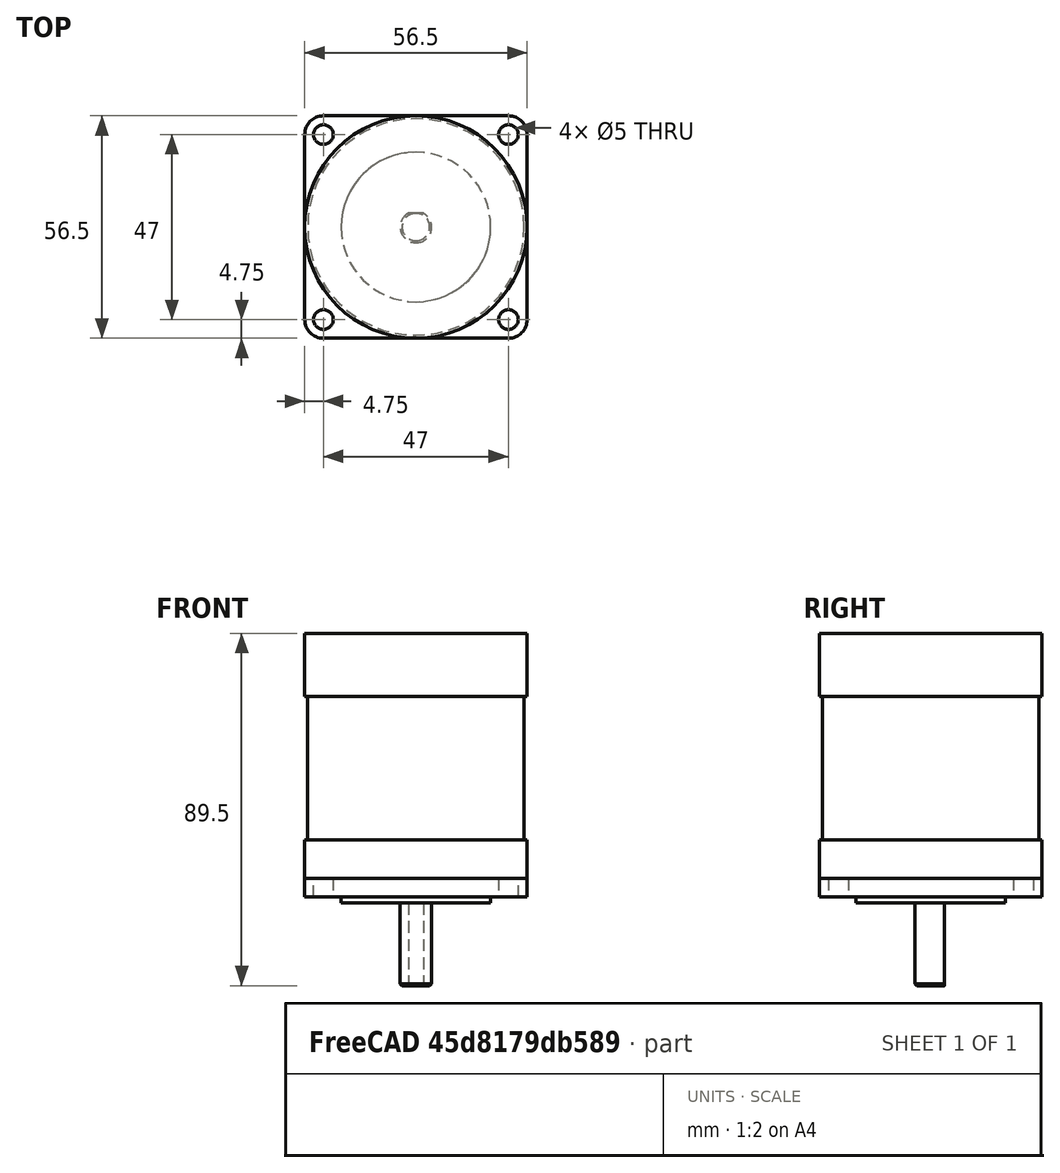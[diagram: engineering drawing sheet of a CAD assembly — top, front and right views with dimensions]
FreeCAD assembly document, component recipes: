
FREECAD ASSEMBLY — COMPONENT RECIPES ("57BLY-0730NBB")

This assembly document has 2 components, labeled P0..P1 below (a component is one placed body or linked part). 2 of them carry a construction recipe — the FreeCAD feature program that regenerates the part from scratch, quoted from this document or its linked companion documents; the rest are supplied as boundary geometry only. No exploded tour is included for this assembly.
COMPONENT P0 — recipe-attached ("57BLY-0730NBB", modeled in this document).
Construction recipe (the document's own serialized feature program — sketch geometry with constraints, then the solid features built on it; lengths are millimeters unless a unit is written):

FEATURE [Sketcher::SketchObject] Sketch
  FullyConstrained = true
  MapMode = 5
  Support = -> [XY_Plane]
  sketch-geometry (9):
    g0: LineSegment StartX=0 StartY=0 StartZ=0 EndX=28.25 EndY=0 EndZ=0
    g1: LineSegment StartX=28.25 StartY=0 StartZ=0 EndX=28.25 EndY=23.5386 EndZ=0
    g2: LineSegment StartX=23.5386 StartY=28.25 StartZ=0 EndX=0 EndY=28.25 EndZ=0
    g3: LineSegment StartX=0 StartY=28.25 StartZ=0 EndX=0 EndY=0 EndZ=0
    g4: ArcOfCircle CenterX=23.5386 CenterY=23.5386 CenterZ=0 NormalX=0 NormalY=0 NormalZ=1 AngleXU=0 Radius=4.71142 StartAngle=0 EndAngle=1.5708
    g5: GeomPoint X=28.25 Y=28.25 Z=0
    g6: Circle CenterX=23.5 CenterY=23.5 CenterZ=0 NormalX=0 NormalY=0 NormalZ=1 AngleXU=0 Radius=2.5
    g7: LineSegment StartX=0 StartY=0 StartZ=0 EndX=28.25 EndY=28.25 EndZ=0
    g8: GeomPoint X=26.8701 Y=26.8701 Z=0
  constraints (22):
    c: Coincident(g0,g1)
    c: Coincident(g2,g3)
    c: Coincident(g3,g0)
    c: Horizontal(g0)
    c: Horizontal(g2)
    c: Vertical(g1)
    c: Vertical(g3)
    c: Coincident(g0,g-1)
    c: Equal(g0,g3)
    c: PointOnObject(g5,g2)
    c: PointOnObject(g5,g1)
    c: Tangent(g2,g4) = -1.5708
    c: Tangent(g1,g4) = -1.5708
    c: Coincident(g7,g0)
    c: Coincident(g7,g5)
    c: PointOnObject(g6,g7)
    c: DistanceX(g6) = 23.5
    c: PointOnObject(g8,g4)
    c: PointOnObject(g8,g7)
    c: Distance(g0,g8) = 38
    c: DistanceX(g0) = 28.25  'width'
    c: Diameter(g6) = 5
FEATURE [PartDesign::Pad] Pad
  Direction = (0,0,1)
  Length = 4.7
  Length2 = 10
  Profile = -> Sketch
  ReferenceAxis = -> Sketch [N_Axis]
  Type = 0
FEATURE [PartDesign::Mirrored] Mirrored
  MirrorPlane = -> Sketch [V_Axis]
FEATURE [PartDesign::Mirrored] Mirrored001
  MirrorPlane = -> Sketch [H_Axis]
FEATURE [PartDesign::MultiTransform] MultiTransform
  BaseFeature = -> Pad
  Originals = -> [Pad]
  Transformations = -> [Mirrored,Mirrored001]
FEATURE [Sketcher::SketchObject] Sketch001
  FullyConstrained = true
  MapMode = 5
  Placement = pos=(0,0,0) rot=(1,0,0;1.5708rad)
  Support = -> [XZ_Plane]
  sketch-geometry (10):
    g0: LineSegment StartX=19 StartY=0 StartZ=0 EndX=28.25 EndY=0 EndZ=0
    g1: LineSegment StartX=28.25 StartY=0 StartZ=0 EndX=28.25 EndY=14.5 EndZ=0
    g2: LineSegment StartX=28.25 StartY=14.5 StartZ=0 EndX=27.5 EndY=14.5 EndZ=0
    g3: LineSegment StartX=27.5 StartY=14.5 StartZ=0 EndX=27.5 EndY=51 EndZ=0
    g4: LineSegment StartX=27.5 StartY=51 StartZ=0 EndX=28.25 EndY=51 EndZ=0
    g5: LineSegment StartX=28.25 StartY=51 StartZ=0 EndX=28.25 EndY=67 EndZ=0
    g6: LineSegment StartX=28.25 StartY=67 StartZ=0 EndX=0 EndY=67 EndZ=0
    g7: LineSegment StartX=0 StartY=67 StartZ=0 EndX=0 EndY=-1.5 EndZ=0
    g8: LineSegment StartX=19 StartY=0 StartZ=0 EndX=19 EndY=-1.5 EndZ=0
    g9: LineSegment StartX=19 StartY=-1.5 StartZ=0 EndX=0 EndY=-1.5 EndZ=0
  constraints (31):
    c: PointOnObject(g0,g-1)
    c: Coincident(g0,g1)
    c: Vertical(g1)
    c: Coincident(g1,g2)
    c: Horizontal(g2)
    c: Coincident(g2,g3)
    c: Vertical(g3)
    c: Coincident(g3,g4)
    c: Horizontal(g4)
    c: Coincident(g4,g5)
    c: Vertical(g5)
    c: Coincident(g5,g6)
    c: PointOnObject(g6,g-2)
    c: Horizontal(g6)
    c: Coincident(g6,g7)
    c: Distance(g1) = 14.5
    c: DistanceX(g2) = 27.5
    c: Distance(g3) = 36.5
    c: Vertical(g4,g1)
    c: Distance(g5) = 16
    c: Distance(g7) = 68.5  'total_height'
    c: Vertical(g8)
    c: Coincident(g9,g8)
    c: Horizontal(g9)
    c: DistanceX(g0) = 28.25
    c: Coincident(g0,g8)
    c: Distance(g9) = 19
    c: PointOnObject(g9,g-2)
    c: Coincident(g7,g9)
    c: DistanceY(g7,g-1) = 1.5  'bearing_height'
    c: Horizontal(g0)
FEATURE [PartDesign::Revolution] Revolution
  Angle = 360
  Axis = (0,-2e-16,1)
  Base = (0,0,0)
  BaseFeature = -> MultiTransform
  Profile = -> Sketch001
  ReferenceAxis = -> Sketch001 [V_Axis]
  Reversed = true
FEATURE [PartDesign::Body] Body
  Group = -> [Sketch,Pad,MultiTransform,Mirrored,Mirrored001,Sketch001,Revolution]
  Origin = -> Origin
  Tip = -> Revolution
FEATURE [Sketcher::SketchObject] Sketch002
  FullyConstrained = true
  MapMode = 5
  Support = -> [XY_Plane002]
  expr: .AttachmentOffset.Base.z = 0
  sketch-geometry (3):
    g0: LineSegment StartX=0 StartY=3.5 StartZ=0 EndX=1.93649 EndY=3.5 EndZ=0
    g1: ArcOfCircle CenterX=0 CenterY=0 CenterZ=0 NormalX=0 NormalY=0 NormalZ=1 AngleXU=0 Radius=4 StartAngle=4.71239 EndAngle=7.34862
    g2: LineSegment StartX=-7e-16 StartY=-4 StartZ=0 EndX=0 EndY=3.5 EndZ=0
  constraints (9):
    c: PointOnObject(g0,g-2)
    c: Horizontal(g0)
    c: Coincident(g1,g-1)
    c: PointOnObject(g1,g-2)
    c: Coincident(g1,g0)
    c: Coincident(g2,g1)
    c: Coincident(g2,g0)
    c: Distance(g2) = 7.5
    c: Diameter(g1) = 8
FEATURE [PartDesign::Pad] Pad001
  Direction = (0,0,1)
  Length = 21
  Length2 = 10
  Profile = -> Sketch002
  ReferenceAxis = -> Sketch002 [N_Axis]
  Reversed = true
  Type = 0
FEATURE [PartDesign::Mirrored] Mirrored002
  BaseFeature = -> Pad001
  MirrorPlane = -> Sketch002 [V_Axis]
  Originals = -> [Pad001]
FEATURE [Sketcher::SketchObject] Sketch003
  FullyConstrained = true
  MapMode = 5
  Placement = pos=(0,0,0) rot=(0.57735,0.57735,0.57735;2.0944rad)
  Support = -> [YZ_Plane002]
  expr: Constraints[8] = -Pad001.Length
  sketch-geometry (3):
    g0: LineSegment StartX=3.5 StartY=-21 StartZ=0 EndX=4 EndY=-20.5 EndZ=0
    g1: LineSegment StartX=4 StartY=-20.5 StartZ=0 EndX=4 EndY=-21 EndZ=0
    g2: LineSegment StartX=4 StartY=-21 StartZ=0 EndX=3.5 EndY=-21 EndZ=0
  constraints (9):
    c: Coincident(g0,g1)
    c: Vertical(g1)
    c: Coincident(g1,g2)
    c: Coincident(g2,g0)
    c: Horizontal(g2)
    c: DistanceX(g0) = 3.5
    c: DistanceX(g0) = 4
    c: Equal(g2,g1)
    c: DistanceY(g1) = -21
FEATURE [PartDesign::Groove] Groove
  Angle = 360
  Axis = (-2e-16,3e-16,1)
  Base = (0,0,0)
  BaseFeature = -> Mirrored002
  Profile = -> Sketch003
  ReferenceAxis = -> Sketch003 [V_Axis]
FEATURE [PartDesign::Body] Body001  label="axis"
  Group = -> [Sketch002,Pad001,Mirrored002,Sketch003,Groove]
  Origin = -> Origin002
  Placement = pos=(0,0,-1.5) rot=(0,0,1;0rad)
  Tip = -> Groove
  expr: .Placement.Base.z = -Sketch001.Constraints.bearing_height
COMPONENT P1 — recipe-attached ("cap", modeled in this document).
Construction recipe (the document's own serialized feature program — sketch geometry with constraints, then the solid features built on it; lengths are millimeters unless a unit is written):

FEATURE [PartDesign::CoordinateSystem] LCS_0  label="end"
  AttacherType = Attacher::AttachEngine3D
  AttachmentOffset = pos=(0,0,-13) rot=(0.707107,-0.707107,0;3.14159rad)
  MapMode = 5
  Placement = pos=(0,0,-13) rot=(0.707107,-0.707107,0;3.14159rad)
  Support = -> [XY_Plane003]
  expr: .AttachmentOffset.Base.z = -Sketch005.Constraints.axis_fuxture_cyl_length
FEATURE [Sketcher::SketchObject] Sketch005
  FullyConstrained = true
  MapMode = 5
  Placement = pos=(0,0,0) rot=(1,0,0;1.5708rad)
  Support = -> [XZ_Plane003]
  sketch-geometry (12):
    g0: LineSegment StartX=0 StartY=22.5 StartZ=0 EndX=6 EndY=22.5 EndZ=0
    g1: LineSegment StartX=6 StartY=22.5 StartZ=0 EndX=6 EndY=5 EndZ=0
    g2: LineSegment StartX=6 StartY=5 StartZ=0 EndX=10.5 EndY=5 EndZ=0
    g3: LineSegment StartX=10.5 StartY=5 StartZ=0 EndX=10.5 EndY=3 EndZ=0
    g4: LineSegment StartX=10.5 StartY=3 StartZ=0 EndX=16 EndY=3 EndZ=0
    g5: LineSegment StartX=16 StartY=3 StartZ=0 EndX=16 EndY=0 EndZ=0
    g6: LineSegment StartX=16 StartY=0 StartZ=0 EndX=10.5 EndY=0 EndZ=0
    g7: LineSegment StartX=10.5 StartY=0 StartZ=0 EndX=10.5 EndY=-13 EndZ=0
    g8: LineSegment StartX=10.5 StartY=-13 StartZ=0 EndX=4 EndY=-13 EndZ=0
    g9: LineSegment StartX=4 StartY=-13 StartZ=0 EndX=4 EndY=3 EndZ=0
    g10: LineSegment StartX=4 StartY=3 StartZ=0 EndX=0 EndY=3 EndZ=0
    g11: LineSegment StartX=0 StartY=3 StartZ=0 EndX=0 EndY=22.5 EndZ=0
  constraints (37):
    c: Horizontal(g0)
    c: Coincident(g0,g1)
    c: Vertical(g1)
    c: Coincident(g1,g2)
    c: Horizontal(g2)
    c: Coincident(g2,g3)
    c: Vertical(g3)
    c: Coincident(g3,g4)
    c: Coincident(g4,g5)
    c: Vertical(g5)
    c: Coincident(g5,g6)
    c: Horizontal(g6)
    c: Coincident(g6,g7)
    c: Vertical(g7)
    c: Coincident(g7,g8)
    c: Horizontal(g8)
    c: Coincident(g8,g9)
    c: Vertical(g9)
    c: Horizontal(g4)
    c: DistanceX(g0) = 6
    c: DistanceX(g2) = 10.5
    c: DistanceX(g4) = 16
    c: DistanceX(g7) = 10.5
    c: DistanceX(g8) = 4
    c: DistanceY(g3,g3) = 2
    c: DistanceY(g3,g0) = 19.5
    c: DistanceY(g5,g5) = 3  'shield_length'
    c: Distance(g7,g6) = 13  'axis_fuxture_cyl_length'
    c: Horizontal(g-1,g6)
    c: DistanceY(g0) = 22.5  'shield_to_end'
    c: PointOnObject(g10,g-2)
    c: Horizontal(g10)
    c: Coincident(g11,g10)
    c: Vertical(g11)
    c: DistanceY(g8,g10) = 16  'axis_length'
    c: Coincident(g9,g10)
    c: Coincident(g11,g0)
FEATURE [PartDesign::Revolution] Revolution001
  Angle = 360
  Axis = (0,-2e-16,1)
  Base = (0,0,0)
  Placement = pos=(0,0,0) rot=(1,0,0;1.5708rad)
  Profile = -> Sketch005
  ReferenceAxis = -> Sketch005 [V_Axis]
  Reversed = true
FEATURE [Sketcher::SketchObject] Sketch006
  AttachmentOffset = pos=(0,-6,20) rot=(0,0,1;0rad)
  FullyConstrained = true
  MapMode = 5
  Placement = pos=(0,-20,-6) rot=(1,0,0;1.5708rad)
  Support = -> [XZ_Plane003]
  expr: .AttachmentOffset.Base.y = -Sketch005.Constraints.axis_fuxture_cyl_length + 7mm
  sketch-geometry (1):
    g0: Circle CenterX=0 CenterY=0 CenterZ=0 NormalX=0 NormalY=0 NormalZ=1 AngleXU=0 Radius=2
  constraints (2):
    c: Coincident(g0,g-1)
    c: Diameter(g0) = 4
FEATURE [PartDesign::Hole] Hole
  BaseFeature = -> Revolution001
  CustomThreadClearance = 0
  Depth = 117.943
  DepthType = 1
  Diameter = 4.2
  DrillForDepth = false
  DrillPoint = 1
  DrillPointAngle = 117
  HoleCutCountersinkAngle = 90
  HoleCutCustomValues = false
  HoleCutDepth = 0
  HoleCutDiameter = 6.1
  HoleCutType = 0
  ModelThread = false
  Placement = pos=(0,0,0) rot=(1,0,0;1.5708rad)
  Profile = -> Sketch006
  Tapered = true
  TaperedAngle = 90
  ThreadClass = 0
  ThreadDepth = 117.943
  ThreadDepthType = 0
  ThreadDirection = 0
  ThreadFit = 0
  ThreadSize = 13
  ThreadType = 1
  Threaded = true
  UseCustomThreadClearance = false
FEATURE [Sketcher::SketchObject] Sketch010
  FullyConstrained = false
  MapMode = 5
  Placement = pos=(0,0,0) rot=(1,0,0;1.5708rad)
  Support = -> [XZ_Plane003]
  sketch-geometry (6):
    g0: LineSegment StartX=9.5 StartY=-0.0613249 StartZ=0 EndX=9.5 EndY=0 EndZ=0
    g1: LineSegment StartX=9.5 StartY=0 StartZ=0 EndX=9.5 EndY=0.0613249 EndZ=0
    g2: LineSegment StartX=9.5 StartY=0.0613249 StartZ=0 EndX=10 EndY=0.35 EndZ=0
    g3: LineSegment StartX=10 StartY=0.35 StartZ=0 EndX=10 EndY=0 EndZ=0
    g4: LineSegment StartX=10 StartY=0 StartZ=0 EndX=10 EndY=-0.35 EndZ=0
    g5: LineSegment StartX=10 StartY=-0.35 StartZ=0 EndX=9.5 EndY=-0.0613249 EndZ=0
  constraints (17):
    c: PointOnObject(g0,g-1)
    c: Vertical(g0)
    c: Coincident(g0,g1)
    c: Vertical(g1)
    c: Coincident(g1,g2)
    c: Coincident(g2,g3)
    c: PointOnObject(g3,g-1)
    c: Vertical(g3)
    c: Coincident(g3,g4)
    c: Vertical(g4)
    c: Coincident(g4,g5)
    c: Coincident(g5,g0)
    c: Equal(g0,g1)
    c: Equal(g4,g3)
    c: DistanceX(g3) = 10
    c: DistanceX(g0,g3) = 0.5
    c: Angle(g-1,g5) = 2.61799
FEATURE [Sketcher::SketchObject] Sketch011
  FullyConstrained = true
  MapMode = 5
  Support = -> [XY_Plane003]
  sketch-geometry (1):
    g0: Circle CenterX=0 CenterY=0 CenterZ=0 NormalX=0 NormalY=0 NormalZ=1 AngleXU=0 Radius=10
  constraints (2):
    c: Coincident(g0,g-1)
    c: Diameter(g0) = 20
FEATURE [PartDesign::CoordinateSystem] Local_CS
  AttacherType = Attacher::AttachEngine3D
  AttachmentOffset = pos=(0,0,3) rot=(0,0,1;0rad)
  MapMode = 5
  Placement = pos=(0,0,3) rot=(0,0,1;0rad)
  Support = -> [XY_Plane003]
  expr: .AttachmentOffset.Base.z = Sketch005.Constraints.axis_length - Sketch005.Constraints.axis_fuxture_cyl_length
FEATURE [PartDesign::CoordinateSystem] disk_fixture
  AttacherType = Attacher::AttachEngine3D
  AttachmentOffset = pos=(0,0,3) rot=(0,0,1;0rad)
  MapMode = 5
  Placement = pos=(0,0,3) rot=(0,0,1;0rad)
  Support = -> [XY_Plane003]
  expr: .AttachmentOffset.Base.z = Sketch005.Constraints.shield_length
FEATURE [Sketcher::SketchObject] Sketch012
  FullyConstrained = true
  MapMode = 5
  Placement = pos=(0,0,0) rot=(1,0,0;1.5708rad)
  Support = -> [XZ_Plane003]
  expr: .Constraints.axis_fuxture_cyl_length = Sketch005.Constraints.axis_fuxture_cyl_length
  expr: .Constraints.shield_length = Sketch005.Constraints.shield_length
  expr: Constraints[22] = Sketch005.Constraints[19]
  expr: Constraints[23] = Sketch005.Constraints[20]
  expr: Constraints[24] = Sketch005.Constraints[21]
  expr: Constraints[25] = Sketch005.Constraints[22]
  expr: Constraints[26] = Sketch005.Constraints[23]
  expr: Constraints[27] = Sketch005.Constraints[24]
  expr: Constraints[28] = Sketch005.Constraints[25]
  sketch-geometry (12):
    g0: Circle CenterX=0 CenterY=18 CenterZ=0 NormalX=0 NormalY=0 NormalZ=1 AngleXU=0 Radius=2
    g1: LineSegment StartX=4 StartY=22.5 StartZ=0 EndX=6 EndY=22.5 EndZ=0
    g2: LineSegment StartX=6 StartY=22.5 StartZ=0 EndX=6 EndY=5 EndZ=0
    g3: LineSegment StartX=6 StartY=5 StartZ=0 EndX=10.5 EndY=5 EndZ=0
    g4: LineSegment StartX=10.5 StartY=5 StartZ=0 EndX=10.5 EndY=3 EndZ=0
    g5: LineSegment StartX=10.5 StartY=3 StartZ=0 EndX=16 EndY=3 EndZ=0
    g6: LineSegment StartX=16 StartY=3 StartZ=0 EndX=16 EndY=0 EndZ=0
    g7: LineSegment StartX=16 StartY=0 StartZ=0 EndX=10.5 EndY=0 EndZ=0
    g8: LineSegment StartX=10.5 StartY=0 StartZ=0 EndX=10.5 EndY=-13 EndZ=0
    g9: LineSegment StartX=10.5 StartY=-13 StartZ=0 EndX=4 EndY=-13 EndZ=0
    g10: LineSegment StartX=4 StartY=-13 StartZ=0 EndX=4 EndY=22.5 EndZ=0
    g11: GeomPoint X=0 Y=16 Z=0
  constraints (36):
    c: PointOnObject(g0,g-2)
    c: Diameter(g0) = 4
    c: Horizontal(g1)
    c: Coincident(g1,g2)
    c: Vertical(g2)
    c: Coincident(g2,g3)
    c: Horizontal(g3)
    c: Coincident(g3,g4)
    c: Vertical(g4)
    c: Coincident(g4,g5)
    c: Coincident(g5,g6)
    c: Vertical(g6)
    c: Coincident(g6,g7)
    c: Horizontal(g7)
    c: Coincident(g7,g8)
    c: Vertical(g8)
    c: Coincident(g8,g9)
    c: Horizontal(g9)
    c: Coincident(g9,g10)
    c: Vertical(g10)
    c: Coincident(g1,g10)
    c: Horizontal(g5)
    c: DistanceX(g1) = 6
    c: DistanceX(g3) = 10.5
    c: DistanceX(g5) = 16
    c: DistanceX(g8) = 10.5
    c: DistanceX(g9) = 4
    c: DistanceY(g4,g4) = 2
    c: DistanceY(g4,g1) = 19.5
    c: DistanceY(g6,g6) = 3  'shield_length'
    c: Distance(g8,g7) = 13  'axis_fuxture_cyl_length'
    c: Horizontal(g-1,g7)
    c: DistanceY(g1) = 22.5  'shield_to_end'
    c: PointOnObject(g11,g-2)
    c: PointOnObject(g11,g0)
    c: DistanceY(g2,g11) = 11
FEATURE [PartDesign::Pocket] Pocket
  BaseFeature = -> Hole
  Direction = (0,1,2e-16)
  Length = 5
  Length2 = 5
  Midplane = true
  Placement = pos=(0,0,0) rot=(1,0,0;1.5708rad)
  Profile = -> Sketch012
  ReferenceAxis = -> Sketch012 [N_Axis]
  Type = 1
FEATURE [PartDesign::Body] cap
  Group = -> [LCS_0,Sketch005,Revolution001,Sketch006,Hole,Sketch010,Sketch011,Local_CS,disk_fixture,Sketch012,Pocket]
  Origin = -> Origin003
  Tip = -> Pocket
PROVENANCE & LICENSES
A FreeCAD (.FCStd) document from a public repository crawl; recipes are the document's own serialized feature recipes (and, for linked parts, companion documents' recipes).
License: as declared in the source repository (recorded in the dataset sidecar).
